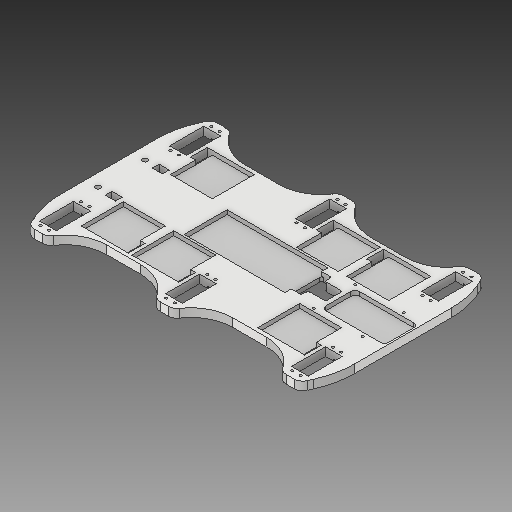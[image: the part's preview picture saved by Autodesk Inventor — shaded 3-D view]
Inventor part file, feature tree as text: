
AUTODESK INVENTOR PART (.ipt)
format: ipt  version: 2017 (Build 210142000, 142)  size: 575,488 bytes
history: native  units: mm
features: extrude x13, sketch x13, fillet x4
ambient origin geometry x8: Origin, YZ Plane, XZ Plane, XY Plane, X Axis, Y Axis, Z Axis, Center Point
bodies: Solid1 (feature_tree)
feature tree (30):
  extrude  "Extrusion1"  Depth=82.5mm
  extrude  "Extrusion2"  Depth=10.0mm
  extrude  "Extrusion3"  Depth=10.0mm
  extrude  "Extrusion4"  Depth=11.5mm
  fillet  "Fillet1"  Radius=5.0mm
  fillet  "Fillet2"  Radius=20.0mm
  extrude  "Extrusion6"  Depth=5.0mm
  extrude  "Extrusion5"  Depth=5.0mm
  extrude  "Extrusion8"  Depth=4.0mm
  fillet  "Fillet3"  Radius=4.0mm
  extrude  "Extrusion10"  Depth=4.5mm
  extrude  "Extrusion11"  Depth=5.0mm
  fillet  "Fillet4"  Radius=5.0mm
  extrude  "Extrusion12"  Depth=6.5mm
  extrude  "Extrusion13"  Depth=2.0mm
  extrude  "Extrusion15"  Depth=10.0mm
  extrude  "Extrusion17"  Depth=2.5mm
  sketch  "Sketch1"  dims[d0=30.0mm d1=82.5mm]
  sketch  "Sketch2"  dims[d2=26.75mm d3=10.0mm]
  sketch  "Sketch3"  dims[d4=120.0mm d5=10.0mm]
  sketch  "Sketch4"  dims[d6=0.0mm d7=11.5mm d8=5.0mm d9=20.0mm]
  sketch  "Sketch5"  dims[d10=40.5mm d11=5.0mm]
  sketch  "Sketch6"  dims[d12=5.0mm d13=5.0mm]
  sketch  "Sketch8"  dims[d14=0.0mm d17=4.0mm d18=4.0mm]
  sketch  "Sketch10"  dims[d19=4.5mm d25=2.75mm]
  sketch  "Sketch11"  dims[d26=2.75mm d27=2.75mm d28=5.0mm]
  sketch  "Sketch12"  dims[d29=0.0mm d30=6.5mm]
  sketch  "Sketch13"  dims[d31=1.2mm d32=2.0mm]
  sketch  "Sketch14"  dims[d33=0.0mm d37=10.0mm]
  sketch  "Sketch16"  dims[d38=50.0mm d40=85.0mm d41=56.0mm d42=2.75mm d43=3.5mm d44=3.5mm d45=3.5mm d46=58.0mm d47=10.0mm d48=0.0mm d49=51.0mm d50=120.0mm d51=5.0mm d52=0.0mm d58=50.0mm d59=50.0mm d61=10.0mm d62=10.0mm d63=10.0mm d64=5.0mm d65=0.0mm d67=3.0mm d68=20.0mm d69=100.0mm d70=3.0mm d71=10.0mm d78=50.0mm d79=36.0mm d80=2.5mm d81=0.0mm d82=40.0mm d83=5.0mm d84=75.0mm d85=5.0mm d86=5.0mm d87=0.0mm d88=36.0mm d89=12.0mm d90=2.0mm d91=20.0mm d92=6.0mm d93=10.0mm d94=0.0mm d95=6.0mm d97=10.0mm d98=0.0mm d99=8.0mm d100=15.0mm d103=5.0mm d104=0.0mm d109=12.0mm d110=10.0mm d111=0.0mm d112=5.0mm d113=2.5mm]
